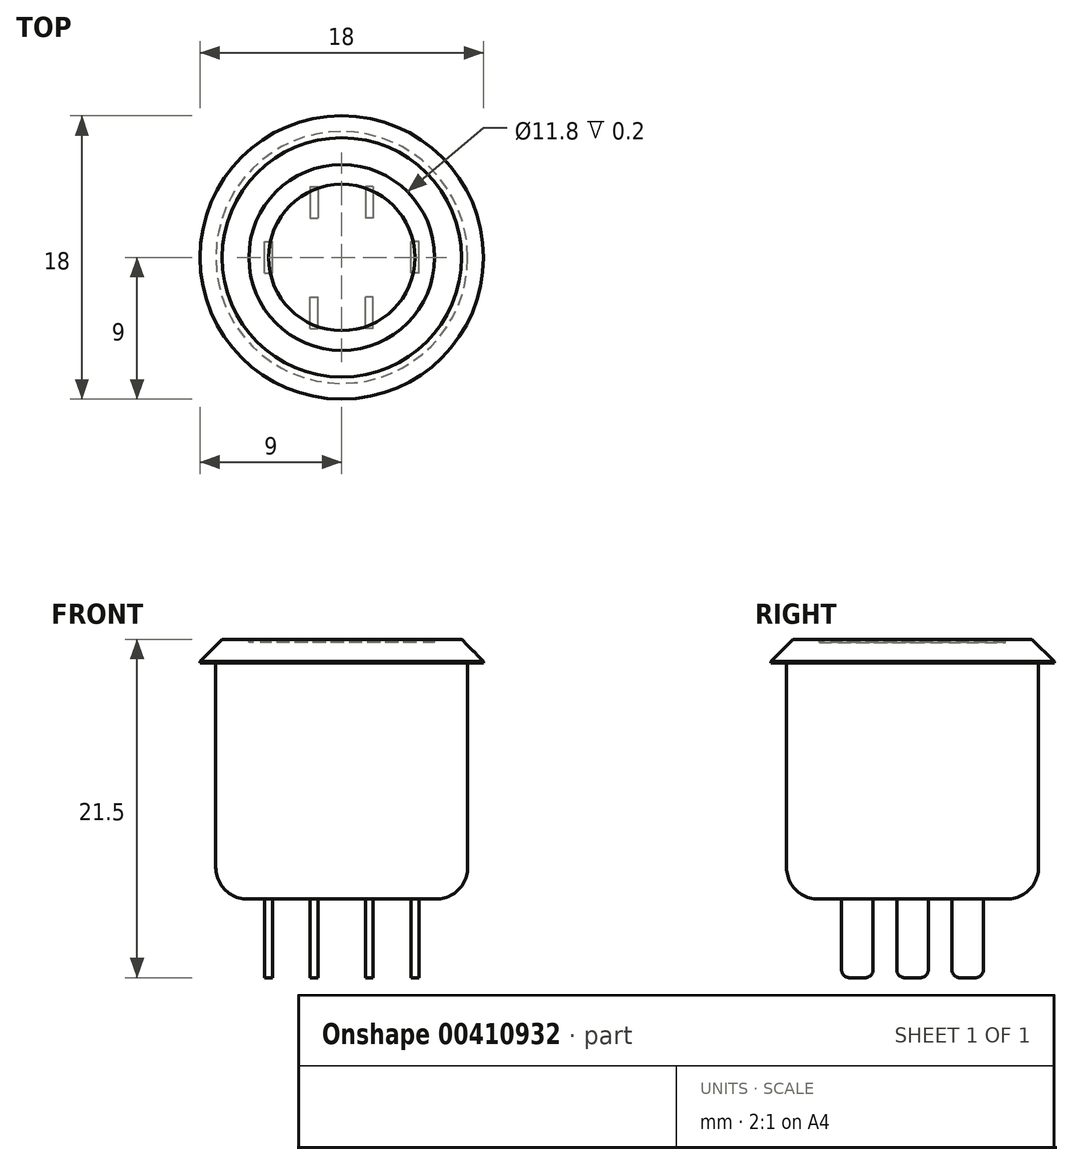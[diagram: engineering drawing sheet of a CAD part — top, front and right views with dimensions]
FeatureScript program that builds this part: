
annotation { "Feature Type Name" : "Feature", "Feature Type Description" : "" }
export const myFeature = defineFeature(function(context is Context, id is Id, definition is map)
    precondition{}
    {
        {
            var Q0;
            Q0=qCreatedBy(makeId("Top.planeOp"),FACE);
            var sketch = newSketch(context, id + "F0", { "sketchPlane" : qUnion([Q0])});
            skCircle(sketch, "E0", {"center": v(0, 0) * mm, "radius": 9 * mm});
            skSolve(sketch);
        }
        {
            var Q0;
            Q0 = qSketchRegion(id + "F0", true);
            extrude(context, id + "F1", {"entities" : qUnion([Q0]), "depth" : 1.5 * mm});
        }
        {
            var Q0;
            Q0=makeQuery(id+"F1.opExtrude","CAP_EDGE",EDGE,{"disambiguationData":[OSD([sQuery(id+"F0.wireOp",EDGE,"E0")])],"isStart":false});
            chamfer(context, id + "F2", {"entities" : qUnion([Q0]), "width" : 1.4 * mm, "tangentPropagation" : true});
        }
        {
            var Q0;
            Q0=makeQuery(id+"F1.opExtrude","CAP_FACE",FACE,{"disambiguationData":[OSD([sQuery(id+"F0.wireOp",EDGE,"E0")])],"isStart":false});
            var sketch = newSketch(context, id + "F3", { "sketchPlane" : qUnion([Q0])});
            skCircle(sketch, "E1", {"center": v(0, 0) * mm, "radius": 4.65 * mm});
            skCircle(sketch, "E2", {"center": v(0, 0) * mm, "radius": 5.9 * mm});
            skSolve(sketch);
        }
        {
            var Q0;
            Q0 = qSketchRegion(id + "F3", true);
            extrude(context, id + "F4", {"entities" : qUnion([Q0]), "operationType" : NewBodyOperationType.REMOVE, "oppositeDirection" : true, "depth" : 0.2 * mm});
        }
        {
            var Q0;
            Q0=makeQuery(id+"F1.opExtrude","CAP_FACE",FACE,{"disambiguationData":[OSD([sQuery(id+"F0.wireOp",EDGE,"E0")])],"isStart":true});
            var sketch = newSketch(context, id + "F5", { "sketchPlane" : qUnion([Q0])});
            skCircle(sketch, "E3", {"center": v(0, 0) * mm, "radius": 8 * mm});
            skSolve(sketch);
        }
        {
            var Q0;
            Q0 = qSketchRegion(id + "F5", true);
            extrude(context, id + "F6", {"entities" : qUnion([Q0]), "operationType" : NewBodyOperationType.ADD, "depth" : 15 * mm});
        }
        {
            var Q0;
            Q0=makeQuery(id+"F6.opExtrude","CAP_EDGE",EDGE,{"disambiguationData":[OSD([sQuery(id+"F5.wireOp",EDGE,"E3")])],"isStart":false});
            fillet(context, id + "F7", {"entities" : qUnion([Q0]), "radius" : 2 * mm, "tangentPropagation" : true, "allowEdgeOverflow" : false});
        }
        {
            var Q0;
            Q0=makeQuery(id+"F6.opExtrude","CAP_FACE",FACE,{"disambiguationData":[OSD([sQuery(id+"F5.wireOp",EDGE,"E3")])],"isStart":false});
            var sketch = newSketch(context, id + "F8", { "sketchPlane" : qUnion([Q0])});
            skLineSegment(sketch, "E4.bottom", {"start": v(-2, 4.5) * mm, "end": v(-1.5, 4.5) * mm});
            skLineSegment(sketch, "E4.top", {"start": v(-2, 2.5) * mm, "end": v(-1.5, 2.5) * mm});
            skLineSegment(sketch, "E4.left", {"start": v(-2, 4.5) * mm, "end": v(-2, 2.5) * mm});
            skLineSegment(sketch, "E4.right", {"start": v(-1.5, 4.5) * mm, "end": v(-1.5, 2.5) * mm});
            skLineSegment(sketch, "E5.MirrorCS", {"start": v(1.5, 4.5) * mm, "end": v(1.5, 2.5) * mm});
            skLineSegment(sketch, "E6.MirrorCS", {"start": v(2, 4.5) * mm, "end": v(1.5, 4.5) * mm});
            skLineSegment(sketch, "E7.MirrorCS", {"start": v(2, 4.5) * mm, "end": v(2, 2.5) * mm});
            skLineSegment(sketch, "E8.MirrorCS", {"start": v(2, 2.5) * mm, "end": v(1.5, 2.5) * mm});
            skLineSegment(sketch, "E9.MirrorCS", {"start": v(2, -2.5) * mm, "end": v(1.5, -2.5) * mm});
            skLineSegment(sketch, "E10.MirrorCS", {"start": v(2, -4.5) * mm, "end": v(2, -2.5) * mm});
            skLineSegment(sketch, "E11.MirrorCS", {"start": v(1.5, -4.5) * mm, "end": v(1.5, -2.5) * mm});
            skLineSegment(sketch, "E12.MirrorCS", {"start": v(2, -4.5) * mm, "end": v(1.5, -4.5) * mm});
            skLineSegment(sketch, "E13.MirrorCS", {"start": v(-1.5, -4.5) * mm, "end": v(-1.5, -2.5) * mm});
            skLineSegment(sketch, "E14.MirrorCS", {"start": v(-2, -2.5) * mm, "end": v(-1.5, -2.5) * mm});
            skLineSegment(sketch, "E15.MirrorCS", {"start": v(-2, -4.5) * mm, "end": v(-2, -2.5) * mm});
            skLineSegment(sketch, "E16.MirrorCS", {"start": v(-2, -4.5) * mm, "end": v(-1.5, -4.5) * mm});
            skLineSegment(sketch, "E17.bottom", {"start": v(-4.9, 1) * mm, "end": v(-4.4, 1) * mm});
            skLineSegment(sketch, "E17.top", {"start": v(-4.9, -1) * mm, "end": v(-4.4, -1) * mm});
            skLineSegment(sketch, "E17.left", {"start": v(-4.9, 1) * mm, "end": v(-4.9, -1) * mm});
            skLineSegment(sketch, "E17.right", {"start": v(-4.4, 1) * mm, "end": v(-4.4, -1) * mm});
            skLineSegment(sketch, "E18.MirrorCS", {"start": v(4.4, 1) * mm, "end": v(4.4, -1) * mm});
            skLineSegment(sketch, "E19.MirrorCS", {"start": v(4.9, 1) * mm, "end": v(4.4, 1) * mm});
            skLineSegment(sketch, "E20.MirrorCS", {"start": v(4.9, 1) * mm, "end": v(4.9, -1) * mm});
            skLineSegment(sketch, "E21.MirrorCS", {"start": v(4.9, -1) * mm, "end": v(4.4, -1) * mm});
            skSolve(sketch);
        }
        {
            var Q0;
            Q0 = qSketchRegion(id + "F8", true);
            extrude(context, id + "F9", {"entities" : qUnion([Q0]), "operationType" : NewBodyOperationType.ADD, "depth" : 5 * mm});
        }
        {
            var Q0;
            Q0=makeQuery(id+"F9.opExtrude","CAP_EDGE",EDGE,{"disambiguationData":[OSD([sQuery(id+"F8.wireOp",EDGE,"E4.bottom")])],"isStart":false});
            var Q1;
            Q1=makeQuery(id+"F9.opExtrude","CAP_EDGE",EDGE,{"disambiguationData":[OSD([sQuery(id+"F8.wireOp",EDGE,"E6.MirrorCS")])],"isStart":false});
            var Q2;
            Q2=makeQuery(id+"F9.opExtrude","CAP_EDGE",EDGE,{"disambiguationData":[OSD([sQuery(id+"F8.wireOp",EDGE,"E19.MirrorCS")])],"isStart":false});
            var Q3;
            Q3=makeQuery(id+"F9.opExtrude","CAP_EDGE",EDGE,{"disambiguationData":[OSD([sQuery(id+"F8.wireOp",EDGE,"E17.bottom")])],"isStart":false});
            var Q4;
            Q4=makeQuery(id+"F9.opExtrude","CAP_EDGE",EDGE,{"disambiguationData":[OSD([sQuery(id+"F8.wireOp",EDGE,"E9.MirrorCS")])],"isStart":false});
            var Q5;
            Q5=makeQuery(id+"F9.opExtrude","CAP_EDGE",EDGE,{"disambiguationData":[OSD([sQuery(id+"F8.wireOp",EDGE,"E14.MirrorCS")])],"isStart":false});
            var Q6;
            Q6=makeQuery(id+"F9.opExtrude","CAP_EDGE",EDGE,{"disambiguationData":[OSD([sQuery(id+"F8.wireOp",EDGE,"E17.top")])],"isStart":false});
            var Q7;
            Q7=makeQuery(id+"F9.opExtrude","CAP_EDGE",EDGE,{"disambiguationData":[OSD([sQuery(id+"F8.wireOp",EDGE,"E4.top")])],"isStart":false});
            var Q8;
            Q8=makeQuery(id+"F9.opExtrude","CAP_EDGE",EDGE,{"disambiguationData":[OSD([sQuery(id+"F8.wireOp",EDGE,"E8.MirrorCS")])],"isStart":false});
            var Q9;
            Q9=makeQuery(id+"F9.opExtrude","CAP_EDGE",EDGE,{"disambiguationData":[OSD([sQuery(id+"F8.wireOp",EDGE,"E21.MirrorCS")])],"isStart":false});
            var Q10;
            Q10=makeQuery(id+"F9.opExtrude","CAP_EDGE",EDGE,{"disambiguationData":[OSD([sQuery(id+"F8.wireOp",EDGE,"E12.MirrorCS")])],"isStart":false});
            var Q11;
            Q11=makeQuery(id+"F9.opExtrude","CAP_EDGE",EDGE,{"disambiguationData":[OSD([sQuery(id+"F8.wireOp",EDGE,"E16.MirrorCS")])],"isStart":false});
            fillet(context, id + "F10", {"entities" : qUnion([Q0, Q1, Q2, Q3, Q4, Q5, Q6, Q7, Q8, Q9, Q10, Q11]), "radius" : 0.5 * mm, "tangentPropagation" : true, "allowEdgeOverflow" : false});
        }
    });
